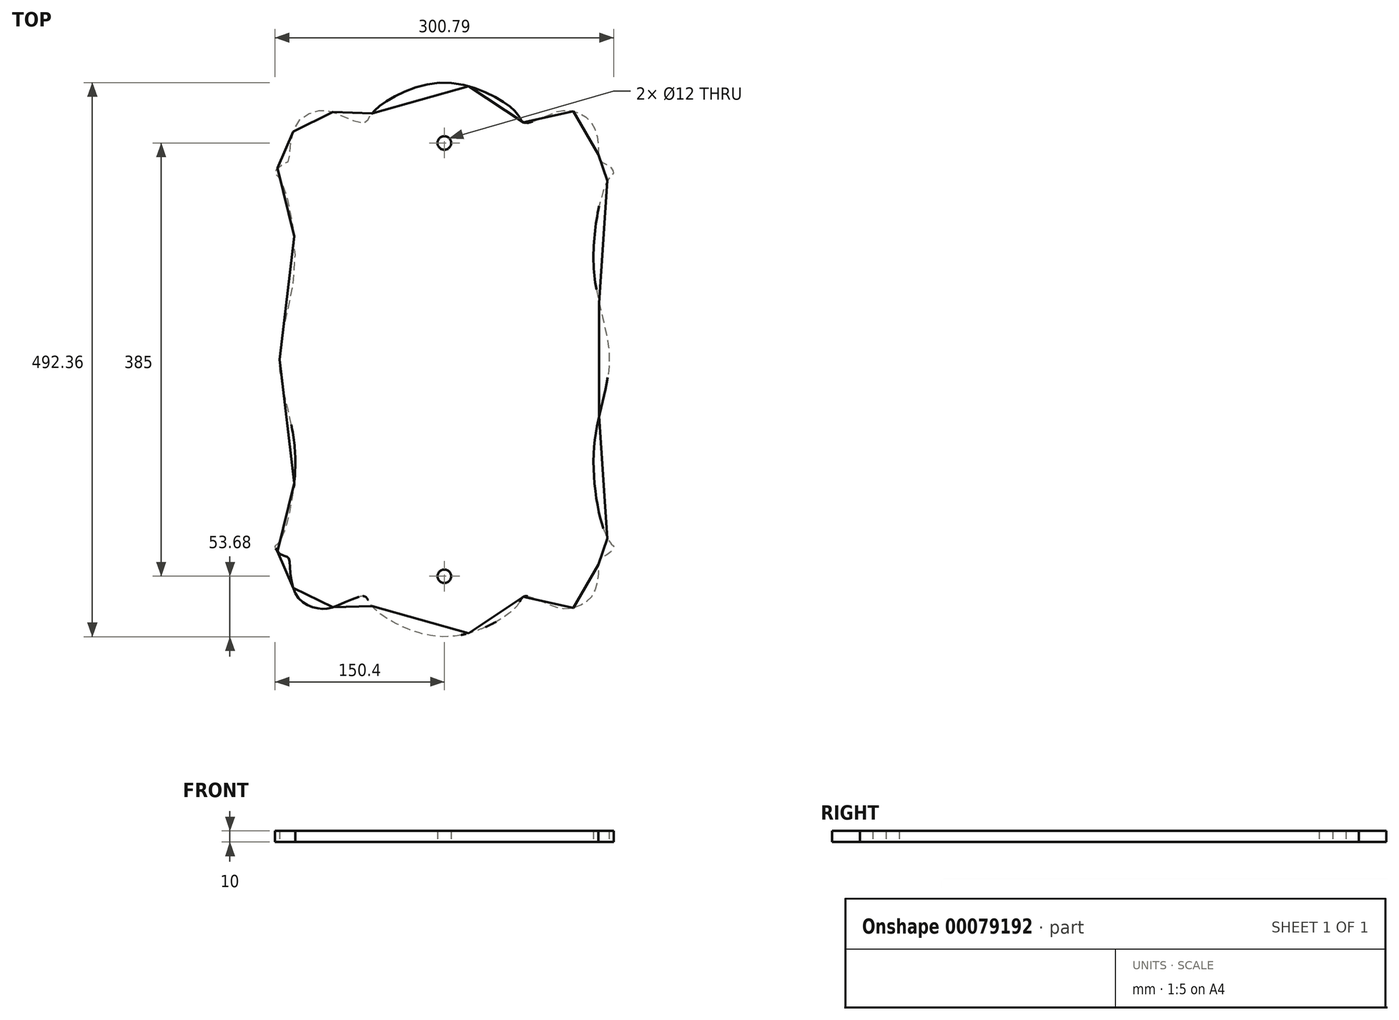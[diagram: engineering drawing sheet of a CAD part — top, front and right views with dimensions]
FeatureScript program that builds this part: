
annotation { "Feature Type Name" : "Feature", "Feature Type Description" : "" }
export const myFeature = defineFeature(function(context is Context, id is Id, definition is map)
    precondition{}
    {
        {
            var Q0;
            Q0=qCreatedBy(makeId("Top.planeOp"),FACE);
            var sketch = newSketch(context, id + "F0", { "sketchPlane" : qUnion([Q0])});
            skPoint(sketch, "E0", {"position": v(150.32, -165.76) * mm});
            skPoint(sketch, "E1", {"position": v(107.37, -221.56) * mm});
            skPoint(sketch, "E2", {"position": v(69.02, -211.72) * mm});
            skPoint(sketch, "E3", {"position": v(0, -246.18) * mm});
            skPoint(sketch, "E4", {"position": v(138.05, -177.25) * mm});
            skPoint(sketch, "E5", {"position": v(146.48, 0) * mm});
            skPoint(sketch, "E6", {"position": v(132.68, -82.88) * mm});
            skLineSegment(sketch, "E7", {"start": v(0, 292) * mm, "end": v(0, -246.18) * mm, "construction": true});
            skPoint(sketch, "E8.MirrorP", {"position": v(-146.48, 0) * mm});
            skPoint(sketch, "E9.MirrorP", {"position": v(-132.68, -82.88) * mm});
            skPoint(sketch, "E10.MirrorP", {"position": v(-150.32, -165.76) * mm});
            skPoint(sketch, "E11.MirrorP", {"position": v(-138.05, -177.25) * mm});
            skPoint(sketch, "E12.MirrorP", {"position": v(-107.37, -221.56) * mm});
            skPoint(sketch, "E13.MirrorP", {"position": v(-69.02, -211.72) * mm});
            skPoint(sketch, "E14", {"position": v(0, 0) * mm});
            skPoint(sketch, "E15", {"position": v(-146.25, -161.4) * mm});
            skPoint(sketch, "E16", {"position": v(-136.87, -189.28) * mm});
            skPoint(sketch, "E17", {"position": v(-146.26, -172.33) * mm});
            skPoint(sketch, "E18", {"position": v(-131.04, -210.06) * mm});
            skPoint(sketch, "E19", {"position": v(-94.82, -218.38) * mm});
            skPoint(sketch, "E20", {"position": v(-60.59, -222.84) * mm});
            skPoint(sketch, "E21", {"position": v(-67.25, -214.49) * mm});
            skPoint(sketch, "E22", {"position": v(-72.48, -210.2) * mm});
            skPoint(sketch, "E23", {"position": v(-119.37, -219.05) * mm});
            skPoint(sketch, "E24", {"position": v(-149.89, -167.68) * mm});
            skPoint(sketch, "E25.MirrorP", {"position": v(60.59, -222.84) * mm});
            skPoint(sketch, "E26.MirrorP", {"position": v(67.25, -214.49) * mm});
            skPoint(sketch, "E27.MirrorP", {"position": v(72.48, -210.2) * mm});
            skPoint(sketch, "E28.MirrorP", {"position": v(94.82, -218.38) * mm});
            skPoint(sketch, "E29.MirrorP", {"position": v(119.37, -219.05) * mm});
            skPoint(sketch, "E30.MirrorP", {"position": v(136.87, -189.28) * mm});
            skPoint(sketch, "E31.MirrorP", {"position": v(146.26, -172.33) * mm});
            skPoint(sketch, "E32.MirrorP", {"position": v(149.89, -167.68) * mm});
            skPoint(sketch, "E33.MirrorP", {"position": v(146.25, -161.4) * mm});
            skPoint(sketch, "E34", {"position": v(-139.73, -175.31) * mm});
            skPoint(sketch, "E35.MirrorP", {"position": v(131.04, -210.06) * mm});
            skPoint(sketch, "E36.MirrorP", {"position": v(-132.68, 82.88) * mm});
            skPoint(sketch, "E37.MirrorP", {"position": v(-139.73, 175.31) * mm});
            skPoint(sketch, "E38.MirrorP", {"position": v(-150.32, 165.76) * mm});
            skPoint(sketch, "E39.MirrorP", {"position": v(69.02, 211.72) * mm});
            skPoint(sketch, "E40.MirrorP", {"position": v(150.32, 165.76) * mm});
            skPoint(sketch, "E41.MirrorP", {"position": v(-67.25, 214.49) * mm});
            skPoint(sketch, "E42.MirrorP", {"position": v(131.04, 210.06) * mm});
            skPoint(sketch, "E43.MirrorP", {"position": v(60.59, 222.84) * mm});
            skPoint(sketch, "E44.MirrorP", {"position": v(119.37, 219.05) * mm});
            skPoint(sketch, "E45.MirrorP", {"position": v(136.87, 189.28) * mm});
            skPoint(sketch, "E46.MirrorP", {"position": v(-72.48, 210.2) * mm});
            skPoint(sketch, "E47.MirrorP", {"position": v(-138.05, 177.25) * mm});
            skPoint(sketch, "E48.MirrorP", {"position": v(-69.02, 211.72) * mm});
            skPoint(sketch, "E49.MirrorP", {"position": v(72.48, 210.2) * mm});
            skPoint(sketch, "E50.MirrorP", {"position": v(-146.25, 161.4) * mm});
            skPoint(sketch, "E51.MirrorP", {"position": v(-136.87, 189.28) * mm});
            skPoint(sketch, "E52.MirrorP", {"position": v(138.05, 177.25) * mm});
            skPoint(sketch, "E53.MirrorP", {"position": v(67.25, 214.49) * mm});
            skPoint(sketch, "E54.MirrorP", {"position": v(-149.89, 167.68) * mm});
            skPoint(sketch, "E55.MirrorP", {"position": v(149.89, 167.68) * mm});
            skPoint(sketch, "E56.MirrorP", {"position": v(-107.37, 221.56) * mm});
            skPoint(sketch, "E57.MirrorP", {"position": v(-94.82, 218.38) * mm});
            skPoint(sketch, "E58.MirrorP", {"position": v(146.26, 172.33) * mm});
            skPoint(sketch, "E59.MirrorP", {"position": v(107.37, 221.56) * mm});
            skPoint(sketch, "E60.MirrorP", {"position": v(-131.04, 210.06) * mm});
            skPoint(sketch, "E61.MirrorP", {"position": v(94.82, 218.38) * mm});
            skPoint(sketch, "E62.MirrorP", {"position": v(146.25, 161.4) * mm});
            skPoint(sketch, "E63.MirrorP", {"position": v(0, 246.18) * mm});
            skPoint(sketch, "E64.MirrorP", {"position": v(-146.26, 172.33) * mm});
            skPoint(sketch, "E65.MirrorP", {"position": v(-119.37, 219.05) * mm});
            skPoint(sketch, "E66.MirrorP", {"position": v(-60.59, 222.84) * mm});
            skPoint(sketch, "E67.MirrorP", {"position": v(132.68, 82.88) * mm});
            skFitSpline(sketch, "E68", {"points": [v(-146.48, 0) * mm, v(-132.68, 82.88) * mm, v(-146.25, 161.4) * mm, v(-150.32, 165.76) * mm, v(-149.89, 167.68) * mm, v(-146.26, 172.33) * mm, v(-139.73, 175.31) * mm, v(-138.05, 177.25) * mm, v(-136.87, 189.28) * mm, v(-131.04, 210.06) * mm, v(-119.37, 219.05) * mm, v(-107.37, 221.56) * mm, v(-94.82, 218.38) * mm, v(-72.48, 210.2) * mm, v(-69.02, 211.72) * mm, v(-67.25, 214.49) * mm, v(-60.59, 222.84) * mm, v(0, 246.18) * mm, v(60.59, 222.84) * mm, v(67.25, 214.49) * mm, v(69.02, 211.72) * mm, v(72.48, 210.2) * mm, v(94.82, 218.38) * mm, v(107.37, 221.56) * mm, v(119.37, 219.05) * mm, v(131.04, 210.06) * mm, v(136.87, 189.28) * mm, v(138.05, 177.25) * mm, v(146.26, 172.33) * mm, v(149.89, 167.68) * mm, v(150.32, 165.76) * mm, v(146.25, 161.4) * mm, v(132.68, 82.88) * mm, v(146.48, 0) * mm, v(132.68, -82.88) * mm, v(146.25, -161.4) * mm, v(150.32, -165.76) * mm, v(149.89, -167.68) * mm, v(146.26, -172.33) * mm, v(138.05, -177.25) * mm, v(136.87, -189.28) * mm, v(131.04, -210.06) * mm, v(119.37, -219.05) * mm, v(107.37, -221.56) * mm, v(94.82, -218.38) * mm, v(72.48, -210.2) * mm, v(69.02, -211.72) * mm, v(67.25, -214.49) * mm, v(60.59, -222.84) * mm, v(0, -246.18) * mm, v(-60.59, -222.84) * mm, v(-67.25, -214.49) * mm, v(-69.02, -211.72) * mm, v(-72.48, -210.2) * mm, v(-94.82, -218.38) * mm, v(-107.37, -221.56) * mm, v(-119.37, -219.05) * mm, v(-131.04, -210.06) * mm, v(-136.87, -189.28) * mm, v(-138.05, -177.25) * mm, v(-139.73, -175.31) * mm, v(-146.26, -172.33) * mm, v(-149.89, -167.68) * mm, v(-150.32, -165.76) * mm, v(-146.25, -161.4) * mm, v(-132.68, -82.88) * mm, v(-146.48, 0) * mm]});
            skPoint(sketch, "E69", {"position": v(0, 295) * mm});
            skPoint(sketch, "E70", {"position": v(-30, 295) * mm});
            skPoint(sketch, "E71", {"position": v(-225, 0) * mm});
            skPoint(sketch, "E72", {"position": v(-225, 100) * mm});
            skPoint(sketch, "E73.MirrorP", {"position": v(225, 100) * mm});
            skPoint(sketch, "E74.MirrorP", {"position": v(225, -60) * mm});
            skLineSegment(sketch, "E75", {"start": v(0, 0) * mm, "end": v(-373.3, 215.53) * mm, "construction": true});
            skLineSegment(sketch, "E76", {"start": v(0, 0) * mm, "end": v(-204.64, 354.44) * mm, "construction": true});
            skLineSegment(sketch, "E77", {"start": v(-225, 0) * mm, "end": v(-225, 100) * mm});
            skLineSegment(sketch, "E78", {"start": v(-30, 295) * mm, "end": v(0, 295) * mm});
            skPoint(sketch, "E79", {"position": v(-30, 100) * mm});
            skArc(sketch, "E80", {"start": v(-30, 295) * mm, "mid": v(-167.89, 237.89) * mm, "end": v(-225, 100) * mm});
            skLineSegment(sketch, "E81.MirrorCS", {"start": v(225, 0) * mm, "end": v(225, 100) * mm});
            skArc(sketch, "E82.MirrorCS", {"start": v(30, 295) * mm, "mid": v(167.89, 237.89) * mm, "end": v(225, 100) * mm});
            skLineSegment(sketch, "E83.MirrorCS", {"start": v(30, 295) * mm, "end": v(0, 295) * mm});
            skArc(sketch, "E84.MirrorCS", {"start": v(-30, -295) * mm, "mid": v(-167.89, -237.89) * mm, "end": v(-225, -100) * mm});
            skLineSegment(sketch, "E85.MirrorCS", {"start": v(-225, 0) * mm, "end": v(-225, -100) * mm});
            skLineSegment(sketch, "E86.MirrorCS", {"start": v(225, 0) * mm, "end": v(225, -100) * mm});
            skArc(sketch, "E87.MirrorCS", {"start": v(30, -295) * mm, "mid": v(167.89, -237.89) * mm, "end": v(225, -100) * mm});
            skLineSegment(sketch, "E88.MirrorCS", {"start": v(30, -295) * mm, "end": v(0, -295) * mm});
            skLineSegment(sketch, "E89.MirrorCS", {"start": v(-30, -295) * mm, "end": v(0, -295) * mm});
            skCircle(sketch, "E90", {"center": v(0, 192.5) * mm, "radius": 6 * mm});
            skCircle(sketch, "E91.MirrorC", {"center": v(0, -192.5) * mm, "radius": 6 * mm});
            skSolve(sketch);
        }
        {
            var Q0;
            Q0=makeQuery(id+"F0.imprint","IMPRINT",FACE,{"disambiguationData":[TD([[makeQuery(id+"F0.imprint","IMPRINT",EDGE,{"derivedFrom":sQuery(id+"F0.wireOp",EDGE,"E68")}),-1.0]])]});
            extrude(context, id + "F1", {"entities" : qUnion([Q0]), "depth" : 10 * mm, "symmetric" : true});
        }
        {
            var Q0;
            Q0=makeQuery(id+"F1.opExtrude","CAP_FACE",FACE,{"disambiguationData":[OSD([sQuery(id+"F0.wireOp",EDGE,"E68"),sQuery(id+"F0.wireOp",EDGE,"E90"),sQuery(id+"F0.wireOp",EDGE,"E91.MirrorC")])],"isStart":false});
            cPlane(context, id + "F2", {"entities" : qUnion([Q0]), "cplaneType" : CPlaneType.OFFSET, "offset" : 50 * mm, "width" : 150 * mm, "height" : 150 * mm});
        }
    });
